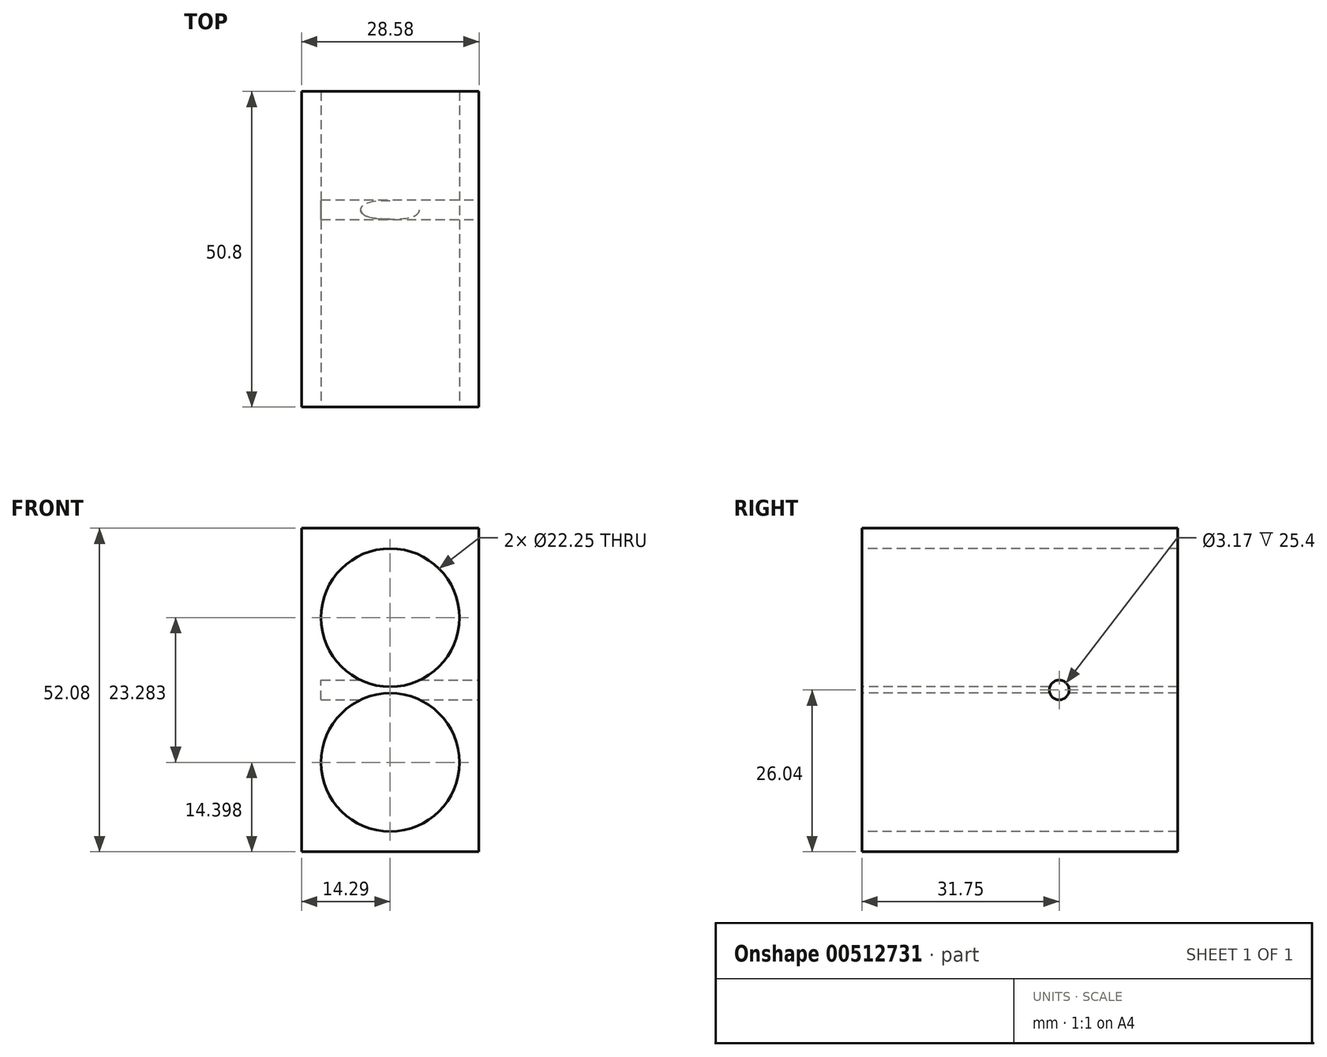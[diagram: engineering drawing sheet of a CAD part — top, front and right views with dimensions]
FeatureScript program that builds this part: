
annotation { "Feature Type Name" : "Feature", "Feature Type Description" : "" }
export const myFeature = defineFeature(function(context is Context, id is Id, definition is map)
    precondition{}
    {
        {
            var Q0;
            Q0=qCreatedBy(makeId("Front.planeOp"),FACE);
            var sketch = newSketch(context, id + "F0", { "sketchPlane" : qUnion([Q0])});
            skLineSegment(sketch, "E0.bottom", {"start": v(-14.29, 26.04) * mm, "end": v(14.29, 26.04) * mm});
            skLineSegment(sketch, "E0.top", {"start": v(-14.29, -26.04) * mm, "end": v(14.29, -26.04) * mm});
            skLineSegment(sketch, "E0.left", {"start": v(-14.29, 26.04) * mm, "end": v(-14.29, -26.04) * mm});
            skLineSegment(sketch, "E0.right", {"start": v(14.29, 26.04) * mm, "end": v(14.29, -26.04) * mm});
            skSolve(sketch);
        }
        {
            var Q0;
            Q0 = qSketchRegion(id + "F0", true);
            extrude(context, id + "F1", {"entities" : qUnion([Q0]), "depth" : 50.8 * mm});
        }
        {
            var Q0;
            Q0=makeQuery(id+"F1.opExtrude","CAP_FACE",FACE,{"disambiguationData":[OSD([sQuery(id+"F0.wireOp",EDGE,"E0.bottom"),sQuery(id+"F0.wireOp",EDGE,"E0.top"),sQuery(id+"F0.wireOp",EDGE,"E0.left"),sQuery(id+"F0.wireOp",EDGE,"E0.right")])],"isStart":false});
            var sketch = newSketch(context, id + "F2", { "sketchPlane" : qUnion([Q0])});
            skCircle(sketch, "E1", {"center": v(0, 11.64) * mm, "radius": 11.13 * mm});
            skCircle(sketch, "E2", {"center": v(0, -11.64) * mm, "radius": 11.13 * mm});
            skSolve(sketch);
        }
        {
            var Q0;
            Q0 = qSketchRegion(id + "F2", true);
            extrude(context, id + "F3", {"entities" : qUnion([Q0]), "operationType" : NewBodyOperationType.REMOVE, "endBound" : BoundingType.THROUGH_ALL, "oppositeDirection" : true, "depth" : 25.4 * mm});
        }
        {
            var Q0;
            Q0=makeQuery(id+"F1.opExtrude","SWEPT_FACE",FACE,{"disambiguationData":[OSD([sQuery(id+"F0.wireOp",EDGE,"E0.right")])]});
            var sketch = newSketch(context, id + "F4", { "sketchPlane" : qUnion([Q0])});
            skCircle(sketch, "E3", {"center": v(-19.05, 0) * mm, "radius": 1.59 * mm});
            skSolve(sketch);
        }
        {
            var Q0;
            Q0 = qSketchRegion(id + "F4", true);
            extrude(context, id + "F5", {"entities" : qUnion([Q0]), "operationType" : NewBodyOperationType.REMOVE, "oppositeDirection" : true, "depth" : 25.4 * mm});
        }
    });
